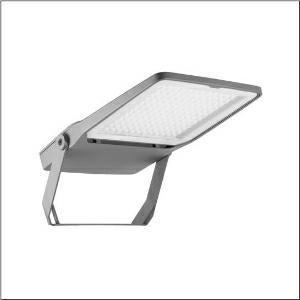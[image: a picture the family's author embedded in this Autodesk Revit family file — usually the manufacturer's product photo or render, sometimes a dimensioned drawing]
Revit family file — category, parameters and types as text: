
# Revit family: floodlight_fl_20_midi___pl43_5xa7681d2a1ac_811e
name_source: partatom
category: Lighting Fixtures
units: mm (PartAtom-declared; Revit-internal decimal feet)

## family parameters
Cut with Voids When Loaded = No
Host = Face
Light Source = No
Part Type = Normal
Room Calculation Point = No
Round Connector Dimension = Use Diameter
Shared = No

## types (1)
- Floodlight FL 20 midi  PL43 (1 x LED 4000K / CRI = 70 (unbekannt), 19080 lm, 4000K)
    Apparent Load = 142 VA
    CIE Flux Codes = 32 74 99 100 100
    Color Rendering = 70
    Color Temperature = 4000K
    Default Elevation = 1800 mm
    Description = Floodlight FL 20 midi, floodlight, primary light control with lens, of plastic, primary optical cover: protective disc, of toughened safety glass, transparent, light distribution: PL43, light emission: direct distribution, primary light characteristic: asymmetric, installation type: surface-mounted, LED High Power LED, rated luminous flux: 19.080 lm, light colour: 740, colour temperature: 4000K, control gear: ECG Basic, control: power reduction, overheat protection, electronic power reduction, with terminal, 5-pole, max. 2.5mm², mains connection: 220..240V, AC, 50/60Hz, rated input power: 142W, LED unit, of diecast aluminium, powder-coated, Siteco® metallic grey (DB 702S), length: 654 mm, width: 450 mm, height: 76mm, housing frame, of diecast aluminium, powder-coated, Siteco® metallic grey (DB 702S), mounting bracket, of steel, powder-coated, Siteco® metallic grey (DB 702S), ON/OFFprotection rating (complete): IP66, insulation class (complete): insulation class I (protective earthing), certification: CE, ENEC, VDE, protection symbol: D, permissible ambient temperature for indoor applications: -40..+40°C, permissible ambient temperature for outdoor applications: -40..+50°C, standard: DIN EN 12944, packaging unit: 1 piece

Light Distribution: PL43
    Height = 76 mm
    Lamp = 1 x LED 4000K / CRI >= 70 (unbekannt)
    Lamp Light Flux = 19080 lm
    Lamp count = 1
    Length = 672 mm
    Luminous efficacy = 134 lm/W
    Manufacturer = Siteco
    ModVariant = No
    Model = 5XA7681D2A1AC
    Number of Poles = 1
    OnlyDefault = Yes
    Power Factor = 1
    Product Name = Floodlight FL 20 midi | PL43
    Product group = floodlight | pylon top
    ProductGroupID = 6101
    Protection Class = Protection class I
    Protection Degree = IP 66
    RLX_Detail_Level = 1
    RlxData = <blob elided: 93905 chars, md5=b7d8c737>
    Socket = socket
    Standby Power = 0 W
    System Light Flux = 19080 lm
    System Power = 142 W
    Type Comments = Product without accessories
    Type Image = l_1005943.jpg
    URL = http://relux.com
    VarID = ---
    Voltage = 0 V
    Weight = 0.00 kg
    Width = 450 mm

## geometry (parser evidence)
native form markers: Blend x4, Sweep x13
no freeform markers — native parametric forms only
